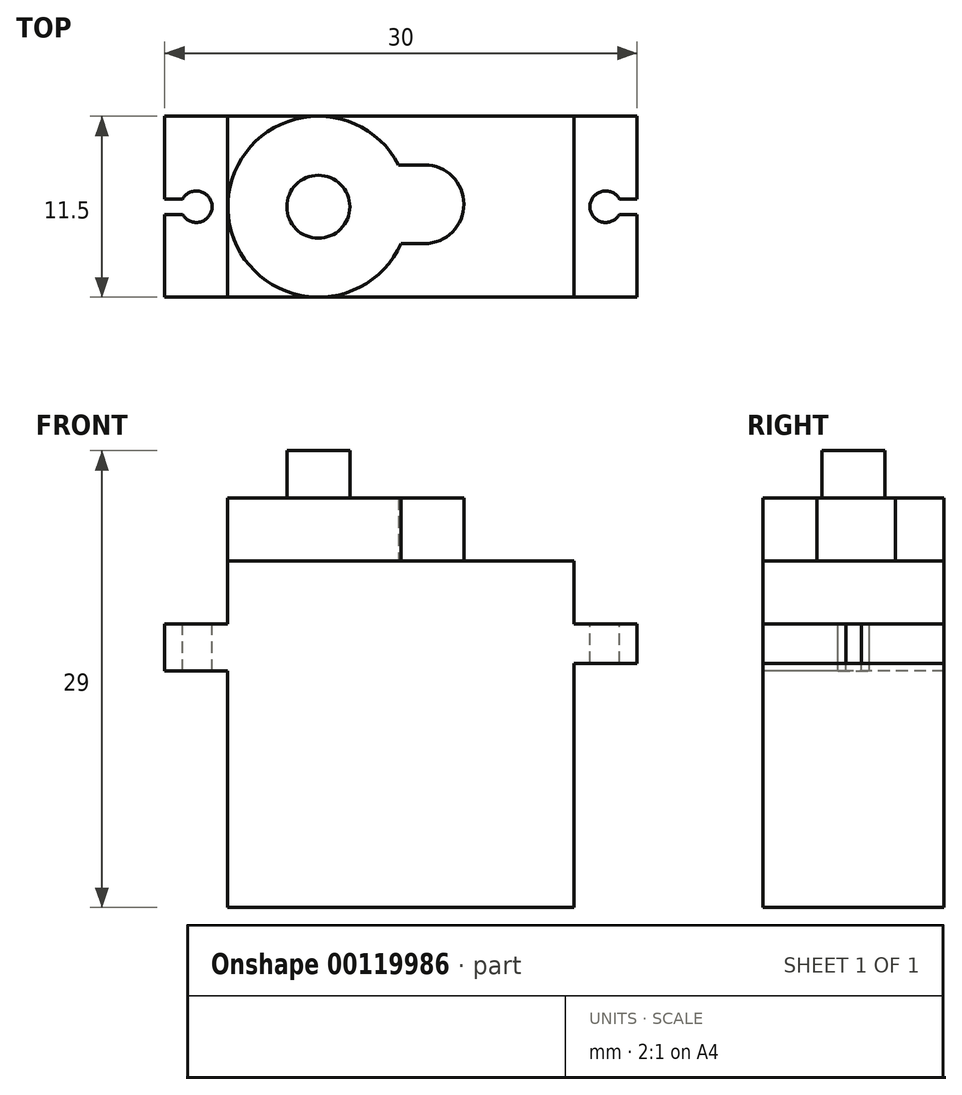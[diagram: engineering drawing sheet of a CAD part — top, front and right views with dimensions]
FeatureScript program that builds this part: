
annotation { "Feature Type Name" : "Feature", "Feature Type Description" : "" }
export const myFeature = defineFeature(function(context is Context, id is Id, definition is map)
    precondition{}
    {
        {
            var Q0;
            Q0=qCreatedBy(makeId("Front.planeOp"),FACE);
            var sketch = newSketch(context, id + "F0", { "sketchPlane" : qUnion([Q0])});
            skLineSegment(sketch, "E0.bottom", {"start": v(0, 0) * mm, "end": v(-22, 0) * mm});
            skLineSegment(sketch, "E0.top", {"start": v(0, 22) * mm, "end": v(-22, 22) * mm});
            skLineSegment(sketch, "E0.left", {"start": v(0, 0) * mm, "end": v(0, 22) * mm});
            skLineSegment(sketch, "E0.right", {"start": v(-22, 0) * mm, "end": v(-22, 22) * mm});
            skSolve(sketch);
        }
        {
            var Q0;
            Q0=makeQuery(id+"F0.imprint","IMPRINT",FACE,{"disambiguationData":[TD([[makeQuery(id+"F0.imprint","IMPRINT",EDGE,{"derivedFrom":sQuery(id+"F0.wireOp",EDGE,"E0.bottom")}),-1.0]])]});
            extrude(context, id + "F1", {"entities" : qUnion([Q0]), "depth" : 11.5 * mm});
        }
        {
            var Q0;
            Q0=makeQuery(id+"F1.opExtrude","SWEPT_FACE",FACE,{"disambiguationData":[OSD([sQuery(id+"F0.wireOp",EDGE,"E0.top")])]});
            var sketch = newSketch(context, id + "F2", { "sketchPlane" : qUnion([Q0])});
            skCircle(sketch, "E1", {"center": v(-16.25, -5.75) * mm, "radius": 5.75 * mm});
            skCircle(sketch, "E2", {"center": v(-9.5, -5.59) * mm, "radius": 2.5 * mm});
            skLineSegment(sketch, "E3", {"start": v(-9.5, -3.09) * mm, "end": v(-11.15, -3.09) * mm});
            skLineSegment(sketch, "E4", {"start": v(-9.5, -8.09) * mm, "end": v(-11, -8.09) * mm});
            skSolve(sketch);
        }
        {
            var Q0;
            {var subQ0=sQuery(id+"F2.wireOp",EDGE,"E1");var subQ5=makeQuery(id+"F2.imprint","INTERSECT",VERTEX,{"derivedFrom":[subQ0,sQuery(id+"F2.wireOp",EDGE,"E3")]});Q0=makeQuery(id+"F2.imprint","IMPRINT",FACE,{"disambiguationData":[TD([[makeQuery(id+"F2.imprint","IMPRINT",EDGE,{"disambiguationData":[TD([[subQ5,1.0]])],"derivedFrom":subQ0}),1.0]])]});}
            var Q1;
            {var subQ0=sQuery(id+"F2.wireOp",EDGE,"E2");var subQ1=sQuery(id+"F2.wireOp",EDGE,"E1");var subQ2=makeQuery(id+"F2.imprint","INTERSECT",VERTEX,{"disambiguationData":[OD(0.0)],"derivedFrom":[subQ1,subQ0]});Q1=makeQuery(id+"F2.imprint","IMPRINT",FACE,{"disambiguationData":[TD([[makeQuery(id+"F2.imprint","IMPRINT",EDGE,{"disambiguationData":[TD([[subQ2,1.0]])],"derivedFrom":subQ1}),1.0]])]});}
            var Q2;
            {var subQ0=sQuery(id+"F2.wireOp",EDGE,"E2");var subQ1=sQuery(id+"F2.wireOp",EDGE,"E1");var subQ2=makeQuery(id+"F2.imprint","INTERSECT",VERTEX,{"disambiguationData":[OD(0.0)],"derivedFrom":[subQ1,subQ0]});Q2=makeQuery(id+"F2.imprint","IMPRINT",FACE,{"disambiguationData":[TD([[makeQuery(id+"F2.imprint","IMPRINT",EDGE,{"disambiguationData":[TD([[subQ2,1.0]])],"derivedFrom":subQ1}),-1.0]])]});}
            var Q3;
            {var subQ0=sQuery(id+"F2.wireOp",EDGE,"E3");Q3=makeQuery(id+"F2.imprint","IMPRINT",FACE,{"disambiguationData":[TD([[makeQuery(id+"F2.imprint","IMPRINT",EDGE,{"derivedFrom":subQ0}),1.0]])]});}
            var Q4;
            {var subQ0=sQuery(id+"F2.wireOp",EDGE,"E4");Q4=makeQuery(id+"F2.imprint","IMPRINT",FACE,{"disambiguationData":[TD([[makeQuery(id+"F2.imprint","IMPRINT",EDGE,{"derivedFrom":subQ0}),-1.0]])]});}
            extrude(context, id + "F3", {"entities" : qUnion([Q0, Q1, Q2, Q3, Q4]), "operationType" : NewBodyOperationType.ADD, "depth" : 4 * mm});
        }
        {
            var Q0;
            Q0=makeQuery(id+"F3.opExtrude","CAP_FACE",FACE,{"disambiguationData":[OSD([sQuery(id+"F2.wireOp",EDGE,"E1"),sQuery(id+"F2.wireOp",EDGE,"E2"),sQuery(id+"F2.wireOp",EDGE,"E3"),sQuery(id+"F2.wireOp",EDGE,"E4")])],"isStart":false});
            var sketch = newSketch(context, id + "F4", { "sketchPlane" : qUnion([Q0])});
            skCircle(sketch, "E5", {"center": v(-16.25, -5.75) * mm, "radius": 2 * mm});
            skSolve(sketch);
        }
        {
            var Q0;
            Q0 = qSketchRegion(id + "F4", true);
            extrude(context, id + "F5", {"entities" : qUnion([Q0]), "operationType" : NewBodyOperationType.ADD, "depth" : 3 * mm});
        }
        {
            var Q0;
            Q0=makeQuery(id+"F1.opExtrude","SWEPT_FACE",FACE,{"disambiguationData":[OSD([sQuery(id+"F0.wireOp",EDGE,"E0.left")])]});
            var sketch = newSketch(context, id + "F6", { "sketchPlane" : qUnion([Q0])});
            skLineSegment(sketch, "E6.bottom", {"start": v(-11.5, 18) * mm, "end": v(0, 18) * mm});
            skLineSegment(sketch, "E6.top", {"start": v(-11.5, 15.5) * mm, "end": v(0, 15.5) * mm});
            skLineSegment(sketch, "E6.left", {"start": v(-11.5, 18) * mm, "end": v(-11.5, 15.5) * mm});
            skLineSegment(sketch, "E6.right", {"start": v(0, 18) * mm, "end": v(0, 15.5) * mm});
            skSolve(sketch);
        }
        {
            var Q0;
            Q0=makeQuery(id+"F6.imprint","IMPRINT",FACE,{"disambiguationData":[TD([[makeQuery(id+"F6.imprint","IMPRINT",EDGE,{"derivedFrom":sQuery(id+"F6.wireOp",EDGE,"E6.bottom")}),-1.0]])]});
            extrude(context, id + "F7", {"entities" : qUnion([Q0]), "operationType" : NewBodyOperationType.ADD, "depth" : 4 * mm});
        }
        {
            var Q0;
            Q0=makeQuery(id+"F1.opExtrude","SWEPT_FACE",FACE,{"disambiguationData":[OSD([sQuery(id+"F0.wireOp",EDGE,"E0.right")])]});
            var sketch = newSketch(context, id + "F8", { "sketchPlane" : qUnion([Q0])});
            skLineSegment(sketch, "E7.bottom", {"start": v(0, 15) * mm, "end": v(11.5, 15) * mm});
            skLineSegment(sketch, "E7.top", {"start": v(0, 18) * mm, "end": v(11.5, 18) * mm});
            skLineSegment(sketch, "E7.left", {"start": v(0, 15) * mm, "end": v(0, 18) * mm});
            skLineSegment(sketch, "E7.right", {"start": v(11.5, 15) * mm, "end": v(11.5, 18) * mm});
            skSolve(sketch);
        }
        {
            var Q0;
            Q0=makeQuery(id+"F8.imprint","IMPRINT",FACE,{"disambiguationData":[TD([[makeQuery(id+"F8.imprint","IMPRINT",EDGE,{"derivedFrom":sQuery(id+"F8.wireOp",EDGE,"E7.bottom")}),1.0]])]});
            extrude(context, id + "F9", {"entities" : qUnion([Q0]), "operationType" : NewBodyOperationType.ADD, "depth" : 4 * mm});
        }
        {
            var Q0;
            Q0=makeQuery(id+"F9.opExtrude","SWEPT_FACE",FACE,{"disambiguationData":[OSD([sQuery(id+"F8.wireOp",EDGE,"E7.top")])]});
            var sketch = newSketch(context, id + "F10", { "sketchPlane" : qUnion([Q0])});
            skCircle(sketch, "E8", {"center": v(-24, -5.75) * mm, "radius": 1 * mm});
            skPoint(sketch, "E8.centerSnap0", {"position": v(-26, -5.75) * mm});
            skLineSegment(sketch, "E9", {"start": v(-24.87, -5.25) * mm, "end": v(-26, -5.25) * mm});
            skLineSegment(sketch, "E10", {"start": v(-24.87, -6.25) * mm, "end": v(-26, -6.25) * mm});
            skSolve(sketch);
        }
        {
            var Q0;
            {var subQ0=sQuery(id+"F10.wireOp",EDGE,"E8");var subQ1=makeQuery(id+"F10.imprint","INTERSECT",VERTEX,{"derivedFrom":[subQ0,sQuery(id+"F10.wireOp",EDGE,"E9")]});Q0=makeQuery(id+"F10.imprint","IMPRINT",FACE,{"disambiguationData":[TD([[makeQuery(id+"F10.imprint","IMPRINT",EDGE,{"disambiguationData":[TD([[subQ1,-1.0]])],"derivedFrom":subQ0}),1.0]])]});}
            var Q1;
            {var subQ0=sQuery(id+"F10.wireOp",EDGE,"E9");Q1=makeQuery(id+"F10.imprint","IMPRINT",FACE,{"disambiguationData":[TD([[makeQuery(id+"F10.imprint","IMPRINT",EDGE,{"derivedFrom":subQ0}),1.0]])]});}
            extrude(context, id + "F11", {"entities" : qUnion([Q0, Q1]), "operationType" : NewBodyOperationType.REMOVE, "oppositeDirection" : true, "depth" : 25.4 * mm});
        }
        {
            var Q0;
            Q0=makeQuery(id+"F7.opExtrude","SWEPT_FACE",FACE,{"disambiguationData":[OSD([sQuery(id+"F6.wireOp",EDGE,"E6.bottom")])]});
            var sketch = newSketch(context, id + "F12", { "sketchPlane" : qUnion([Q0])});
            skCircle(sketch, "E11", {"center": v(2, -5.75) * mm, "radius": 1 * mm});
            skPoint(sketch, "E11.centerSnap0", {"position": v(4, -5.75) * mm});
            skLineSegment(sketch, "E12", {"start": v(2.87, -6.25) * mm, "end": v(4, -6.25) * mm});
            skLineSegment(sketch, "E13", {"start": v(2.87, -5.25) * mm, "end": v(4, -5.25) * mm});
            skSolve(sketch);
        }
        {
            var Q0;
            {var subQ0=sQuery(id+"F12.wireOp",EDGE,"E11");var subQ1=makeQuery(id+"F12.imprint","INTERSECT",VERTEX,{"derivedFrom":[subQ0,sQuery(id+"F12.wireOp",EDGE,"E12")]});Q0=makeQuery(id+"F12.imprint","IMPRINT",FACE,{"disambiguationData":[TD([[makeQuery(id+"F12.imprint","IMPRINT",EDGE,{"disambiguationData":[TD([[subQ1,1.0]])],"derivedFrom":subQ0}),1.0]])]});}
            var Q1;
            {var subQ0=sQuery(id+"F12.wireOp",EDGE,"E12");Q1=makeQuery(id+"F12.imprint","IMPRINT",FACE,{"disambiguationData":[TD([[makeQuery(id+"F12.imprint","IMPRINT",EDGE,{"derivedFrom":subQ0}),1.0]])]});}
            extrude(context, id + "F13", {"entities" : qUnion([Q0, Q1]), "operationType" : NewBodyOperationType.REMOVE, "oppositeDirection" : true, "depth" : 25.4 * mm});
        }
    });
